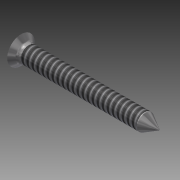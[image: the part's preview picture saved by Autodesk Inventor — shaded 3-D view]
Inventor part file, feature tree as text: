
AUTODESK INVENTOR PART (.ipt)
format: ipt  version: 2014 SP1 (Build 180222100, 222)  size: 147,968 bytes
history: native  units: mm
features: sketch x2, revolve x1, thread x1, extrude x1
ambient origin geometry x8: Origin, YZ Plane, XZ Plane, XY Plane, X Axis, Y Axis, Z Axis, Center Point
bodies: Volumenkörper1 (feature_tree)
feature tree (5):
  revolve  "Umdrehung1"
  thread  "Gewinde1"  [1 undecoded]
  extrude  "Extrusion2"  Depth=1.0mm
  sketch  "Skizze1"  dims[d23=25.0mm d32=1.0mm]
  sketch  "Skizze2"  dims[d41=90.0deg d46=21.0mm d47=0.0mm d48=0.8mm d49=0.8mm d52=1.5mm d53=135.0deg d54=2.5mm d55=30.0deg d56=1.8mm d57=1.8mm d58=1.8mm d59=1.8mm d61=0.8mm d62=0.8mm d63=0.4mm d64=0.4mm d65=0.4mm d66=0.4mm d67=0.6mm d68=0.0mm]
note: 1 required parameter value undecoded (feature->parameter linkage not recoverable at this tier; creation-order binding heuristic only, values carry confidence <= 0.55)
